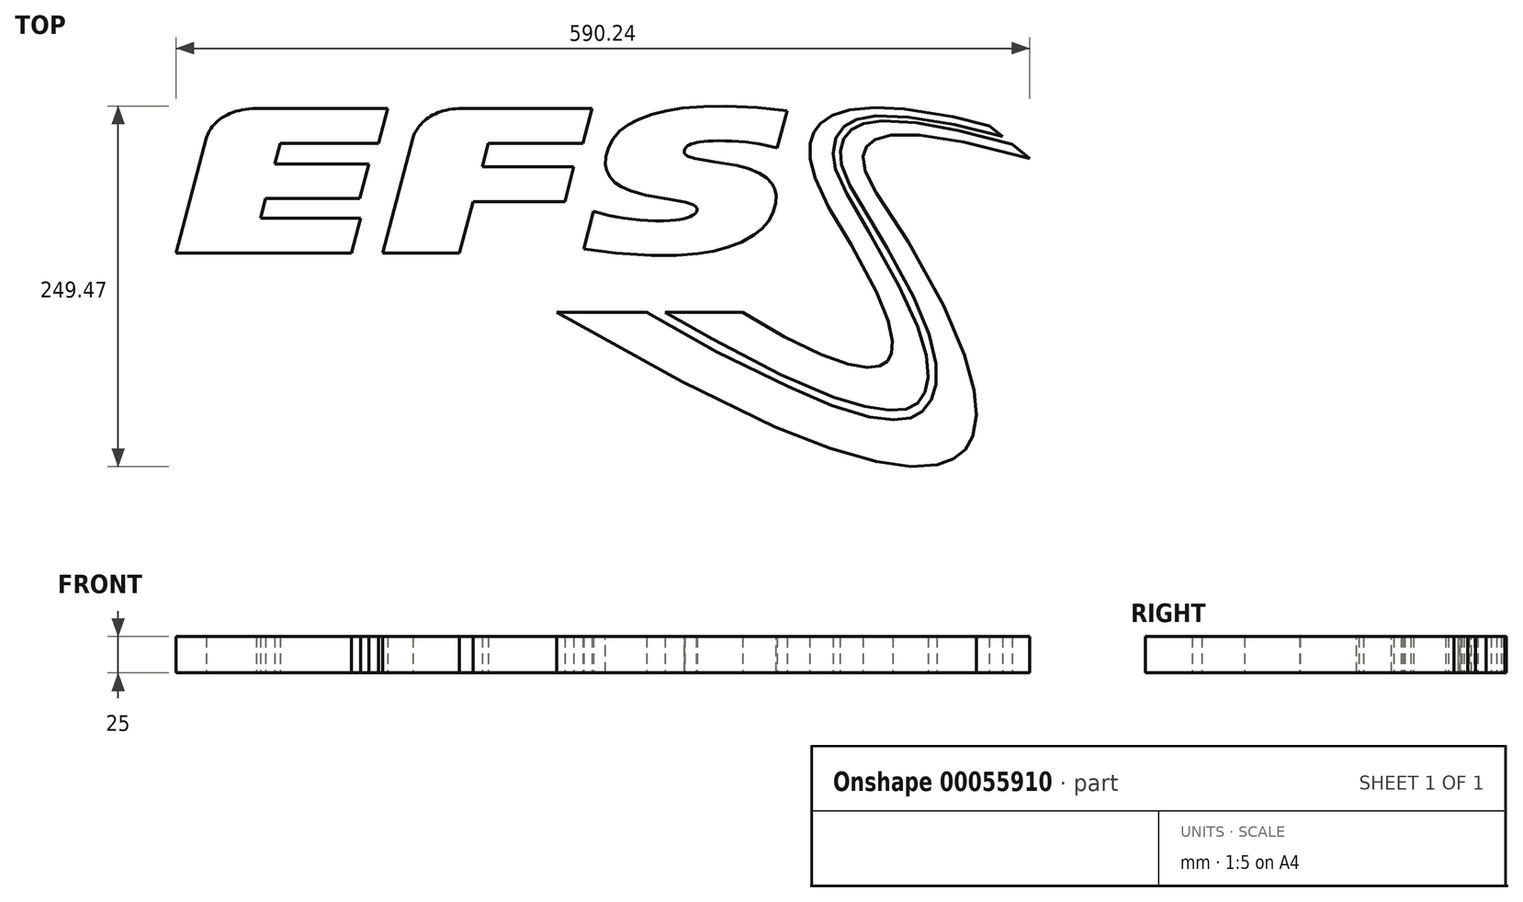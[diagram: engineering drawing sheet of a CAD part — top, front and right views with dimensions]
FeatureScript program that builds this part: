
annotation { "Feature Type Name" : "Feature", "Feature Type Description" : "" }
export const myFeature = defineFeature(function(context is Context, id is Id, definition is map)
    precondition{}
    {
        {
            var Q0;
            Q0=qCreatedBy(makeId("Top.planeOp"),FACE);
            var sketch = newSketch(context, id + "F0", { "sketchPlane" : qUnion([Q0])});
            skLineSegment(sketch, "E0", {"start": v(65.1, 53.07) * mm, "end": v(65.1, 53.21) * mm});
            skLineSegment(sketch, "E1", {"start": v(64.73, 51.46) * mm, "end": v(64.82, 51.68) * mm, "construction": true});
            skLineSegment(sketch, "E2", {"start": v(64.71, 54.56) * mm, "end": v(64.64, 54.68) * mm});
            skLineSegment(sketch, "E3", {"start": v(56.2, 92.99) * mm, "end": v(56.2, 92.8) * mm});
            skLineSegment(sketch, "E4", {"start": v(58.19, 96.78) * mm, "end": v(57.94, 96.57) * mm, "construction": true});
            skLineSegment(sketch, "E5", {"start": v(64.35, 50.82) * mm, "end": v(64.49, 51.03) * mm, "construction": true});
            skLineSegment(sketch, "E6", {"start": v(218.22, -88.53) * mm, "end": v(217.7, -88.86) * mm, "construction": true});
            skLineSegment(sketch, "E7", {"start": v(56.2, 93.18) * mm, "end": v(56.2, 92.99) * mm, "construction": true});
            skLineSegment(sketch, "E8", {"start": v(56.26, 92.44) * mm, "end": v(56.3, 92.26) * mm, "construction": true});
            skLineSegment(sketch, "E9", {"start": v(197.87, -50.41) * mm, "end": v(197.38, -51.11) * mm, "construction": true});
            skLineSegment(sketch, "E10", {"start": v(64.64, 54.68) * mm, "end": v(64.55, 54.8) * mm, "construction": true});
            skLineSegment(sketch, "E11", {"start": v(59.82, 89.37) * mm, "end": v(60.42, 89.17) * mm, "construction": true});
            skLineSegment(sketch, "E12", {"start": v(64.26, 55.14) * mm, "end": v(64.03, 55.36) * mm, "construction": true});
            skLineSegment(sketch, "E13", {"start": v(183.27, 97.87) * mm, "end": v(183.84, 98.45) * mm, "construction": true});
            skLineSegment(sketch, "E14", {"start": v(56.68, 91.43) * mm, "end": v(56.8, 91.28) * mm, "construction": true});
            skLineSegment(sketch, "E15", {"start": v(143.44, 98.9) * mm, "end": v(143.24, 97.48) * mm, "construction": true});
            skLineSegment(sketch, "E16", {"start": v(164.1, 89.26) * mm, "end": v(164.2, 88.02) * mm, "construction": true});
            skLineSegment(sketch, "E17", {"start": v(56.5, 91.75) * mm, "end": v(56.58, 91.6) * mm, "construction": true});
            skLineSegment(sketch, "E18", {"start": v(56.22, 93.37) * mm, "end": v(56.2, 93.18) * mm, "construction": true});
            skLineSegment(sketch, "E19", {"start": v(56.58, 91.6) * mm, "end": v(56.68, 91.43) * mm});
            skLineSegment(sketch, "E20", {"start": v(225.72, -81.26) * mm, "end": v(225.42, -81.7) * mm, "construction": true});
            skLineSegment(sketch, "E21", {"start": v(56.35, 92.09) * mm, "end": v(56.42, 91.92) * mm, "construction": true});
            skLineSegment(sketch, "E22", {"start": v(65, 53.91) * mm, "end": v(64.95, 54.05) * mm, "construction": true});
            skLineSegment(sketch, "E23", {"start": v(173.1, 109.2) * mm, "end": v(172.2, 108.55) * mm, "construction": true});
            skLineSegment(sketch, "E24", {"start": v(182.26, 96.65) * mm, "end": v(182.74, 97.27) * mm, "construction": true});
            skLineSegment(sketch, "E25", {"start": v(56.92, 91.13) * mm, "end": v(57.05, 90.98) * mm, "construction": true});
            skLineSegment(sketch, "E26", {"start": v(200.24, -42.97) * mm, "end": v(200.11, -44.08) * mm, "construction": true});
            skLineSegment(sketch, "E27", {"start": v(196.83, -51.76) * mm, "end": v(196.25, -52.37) * mm, "construction": true});
            skLineSegment(sketch, "E28", {"start": v(64.95, 54.05) * mm, "end": v(64.9, 54.18) * mm, "construction": true});
            skLineSegment(sketch, "E29", {"start": v(63.65, 50.04) * mm, "end": v(63.84, 50.23) * mm, "construction": true});
            skLineSegment(sketch, "E30", {"start": v(56.2, 92.8) * mm, "end": v(56.23, 92.62) * mm, "construction": true});
            skLineSegment(sketch, "E31", {"start": v(56.42, 91.92) * mm, "end": v(56.5, 91.75) * mm, "construction": true});
            skLineSegment(sketch, "E32", {"start": v(56.33, 93.97) * mm, "end": v(56.28, 93.77) * mm});
            skLineSegment(sketch, "E33", {"start": v(184.44, 98.99) * mm, "end": v(185.08, 99.5) * mm, "construction": true});
            skLineSegment(sketch, "E34", {"start": v(64.49, 51.03) * mm, "end": v(64.61, 51.24) * mm, "construction": true});
            skLineSegment(sketch, "E35", {"start": v(-239.63, 122.91) * mm, "end": v(-148.92, 122.91) * mm});
            skLineSegment(sketch, "E36", {"start": v(-155.24, 98.84) * mm, "end": v(-223.24, 98.84) * mm});
            skLineSegment(sketch, "E37", {"start": v(-223.24, 98.84) * mm, "end": v(-226.97, 84.66) * mm});
            skLineSegment(sketch, "E38", {"start": v(-226.97, 84.66) * mm, "end": v(-161.94, 84.66) * mm});
            skLineSegment(sketch, "E39", {"start": v(-155.24, 98.84) * mm, "end": v(-148.92, 122.91) * mm});
            skLineSegment(sketch, "E40", {"start": v(-161.94, 84.66) * mm, "end": v(-168.25, 60.6) * mm});
            skLineSegment(sketch, "E41", {"start": v(-233.28, 60.6) * mm, "end": v(-168.25, 60.6) * mm});
            skLineSegment(sketch, "E42", {"start": v(-233.28, 60.6) * mm, "end": v(-236.85, 46.98) * mm});
            skLineSegment(sketch, "E43", {"start": v(-236.85, 46.98) * mm, "end": v(-167.46, 46.98) * mm});
            skLineSegment(sketch, "E44", {"start": v(-167.46, 46.98) * mm, "end": v(-173.78, 22.91) * mm});
            skLineSegment(sketch, "E45", {"start": v(-173.78, 22.91) * mm, "end": v(-295.12, 22.91) * mm});
            skLineSegment(sketch, "E46", {"start": v(-295.12, 22.91) * mm, "end": v(-274.22, 102.5) * mm});
            skFitSpline(sketch, "E47", {"points": [v(-274.22, 102.5) * mm, v(-273.86, 103.54) * mm, v(-273.35, 104.78) * mm, v(-272.67, 106.18) * mm, v(-271.8, 107.72) * mm, v(-270.74, 109.35) * mm, v(-269.44, 111.03) * mm, v(-267.9, 112.74) * mm, v(-266.09, 114.43) * mm, v(-264, 116.06) * mm, v(-262.83, 116.85) * mm, v(-261.59, 117.6) * mm, v(-260.27, 118.33) * mm, v(-258.86, 119.02) * mm, v(-255.78, 120.28) * mm, v(-252.34, 121.33) * mm, v(-248.52, 122.14) * mm, v(-244.29, 122.69) * mm, v(-239.63, 122.91) * mm], "startDerivative": vector(8.9, 26.32) * mm, "endDerivative": vector(59.2, 1.98) * mm});
            skLineSegment(sketch, "E48", {"start": v(-99.73, 122.91) * mm, "end": v(-7.5, 122.91) * mm});
            skLineSegment(sketch, "E49", {"start": v(-7.5, 122.91) * mm, "end": v(-13.82, 98.84) * mm});
            skLineSegment(sketch, "E50", {"start": v(-13.82, 98.84) * mm, "end": v(-79.24, 98.84) * mm});
            skLineSegment(sketch, "E51", {"start": v(-79.24, 98.84) * mm, "end": v(-83.5, 82.66) * mm});
            skLineSegment(sketch, "E52", {"start": v(-83.5, 82.66) * mm, "end": v(-20.05, 82.66) * mm});
            skLineSegment(sketch, "E53", {"start": v(-20.05, 82.66) * mm, "end": v(-26.37, 58.59) * mm});
            skLineSegment(sketch, "E54", {"start": v(-26.37, 58.59) * mm, "end": v(-89.8, 58.59) * mm});
            skLineSegment(sketch, "E55", {"start": v(-89.8, 58.59) * mm, "end": v(-99.17, 22.91) * mm});
            skLineSegment(sketch, "E56", {"start": v(-99.17, 22.91) * mm, "end": v(-152.3, 22.91) * mm});
            skLineSegment(sketch, "E57", {"start": v(-152.3, 22.91) * mm, "end": v(-131.38, 102.62) * mm});
            skFitSpline(sketch, "E58", {"points": [v(-131.38, 102.62) * mm, v(-131.03, 103.62) * mm, v(-130.55, 104.8) * mm, v(-129.91, 106.13) * mm, v(-129.1, 107.6) * mm, v(-128.11, 109.15) * mm, v(-126.91, 110.76) * mm, v(-125.49, 112.4) * mm, v(-123.83, 114.02) * mm, v(-121.9, 115.62) * mm, v(-119.7, 117.13) * mm, v(-117.21, 118.55) * mm, v(-114.4, 119.83) * mm, v(-111.27, 120.93) * mm, v(-107.8, 121.84) * mm, v(-103.95, 122.51) * mm, v(-99.73, 122.91) * mm], "startDerivative": vector(8, 23.62) * mm, "endDerivative": vector(51.53, 4.1) * mm});
            skLineSegment(sketch, "E59", {"start": v(127.3, 121.2) * mm, "end": v(120.58, 95.55) * mm});
            skLineSegment(sketch, "E60", {"start": v(-6.48, 51.85) * mm, "end": v(-13.28, 25.92) * mm});
            skFitSpline(sketch, "E61", {"points": [v(-6.48, 51.85) * mm, v(-1.42, 50.3) * mm, v(3.92, 48.97) * mm, v(15.43, 46.91) * mm, v(27.44, 45.68) * mm, v(39.38, 45.26) * mm, v(48.5, 45.62) * mm, v(52.63, 46.1) * mm, v(56.35, 46.84) * mm, v(58.02, 47.3) * mm, v(59.55, 47.8) * mm, v(60.93, 48.37) * mm, v(62.16, 48.99) * mm, v(62.72, 49.32) * mm, v(63.2, 49.67) * mm, v(63.65, 50.04) * mm, v(63.84, 50.23) * mm, v(64.03, 50.42) * mm, v(64.2, 50.62) * mm, v(64.35, 50.82) * mm, v(64.49, 51.03) * mm, v(64.61, 51.24) * mm, v(64.73, 51.46) * mm, v(64.82, 51.68) * mm, v(64.9, 51.91) * mm, v(64.97, 52.14) * mm, v(65.04, 52.46) * mm, v(65.09, 52.77) * mm, v(65.1, 53.07) * mm, v(65.1, 53.21) * mm, v(65.1, 53.36) * mm, v(65.08, 53.5) * mm, v(65.06, 53.64) * mm, v(65.03, 53.78) * mm, v(65, 53.91) * mm, v(64.95, 54.05) * mm, v(64.9, 54.18) * mm, v(64.84, 54.3) * mm, v(64.78, 54.43) * mm, v(64.71, 54.56) * mm, v(64.64, 54.68) * mm, v(64.55, 54.8) * mm, v(64.46, 54.92) * mm, v(64.26, 55.14) * mm, v(64.03, 55.36) * mm, v(63.78, 55.57) * mm, v(63.5, 55.78) * mm, v(63.19, 55.97) * mm, v(62.85, 56.15) * mm, v(61.33, 56.84) * mm, v(59.56, 57.48) * mm, v(57.54, 58.06) * mm, v(55.27, 58.59) * mm, v(44.16, 60.45) * mm, v(31.36, 62.67) * mm, v(25, 64.2) * mm, v(18.86, 66.04) * mm, v(15.97, 67.13) * mm, v(13.3, 68.4) * mm, v(12.07, 69.1) * mm, v(10.88, 69.85) * mm, v(9.76, 70.64) * mm, v(8.69, 71.48) * mm, v(7.69, 72.37) * mm, v(6.76, 73.3) * mm, v(5.9, 74.28) * mm, v(5.1, 75.31) * mm, v(4.4, 76.4) * mm, v(3.75, 77.53) * mm, v(3.18, 78.7) * mm, v(2.68, 79.93) * mm, v(2.46, 80.57) * mm, v(2.27, 81.22) * mm, v(2.12, 81.9) * mm, v(1.99, 82.58) * mm, v(1.82, 84.02) * mm, v(1.77, 85.52) * mm, v(1.83, 87.1) * mm, v(2.02, 88.75) * mm, v(2.32, 90.47) * mm, v(2.74, 92.26) * mm, v(3.5, 94.77) * mm, v(4.45, 97.17) * mm, v(5.56, 99.44) * mm, v(6.85, 101.59) * mm, v(8.32, 103.61) * mm, v(9.96, 105.51) * mm, v(11.77, 107.29) * mm, v(13.77, 108.95) * mm, v(15.9, 110.5) * mm, v(18.1, 111.95) * mm, v(20.42, 113.31) * mm, v(22.83, 114.59) * mm, v(27.92, 116.86) * mm, v(33.4, 118.76) * mm, v(39.15, 120.34) * mm, v(45.1, 121.64) * mm, v(51.25, 122.67) * mm, v(57.6, 123.41) * mm, v(70.26, 124.33) * mm, v(82.42, 124.63) * mm, v(105.27, 123.7) * mm, v(127.3, 121.2) * mm], "startDerivative": vector(316.89, -99.49) * mm, "endDerivative": vector(641.52, -85.36) * mm});
            skFitSpline(sketch, "E62", {"points": [v(120.58, 95.55) * mm, v(111.83, 97.6) * mm, v(102.2, 99.2) * mm, v(91.84, 100.23) * mm, v(80.86, 100.57) * mm, v(73.68, 100.42) * mm, v(69.77, 100.15) * mm, v(66.04, 99.63) * mm, v(64.28, 99.27) * mm, v(62.63, 98.83) * mm, v(61.1, 98.3) * mm, v(59.68, 97.7) * mm, v(59.04, 97.36) * mm, v(58.74, 97.18) * mm, v(58.45, 96.98) * mm, v(58.19, 96.78) * mm, v(57.94, 96.57) * mm, v(57.7, 96.35) * mm, v(57.48, 96.12) * mm, v(57.28, 95.89) * mm, v(57.1, 95.64) * mm, v(56.93, 95.38) * mm, v(56.77, 95.12) * mm, v(56.64, 94.85) * mm, v(56.52, 94.56) * mm, v(56.41, 94.27) * mm, v(56.33, 93.97) * mm, v(56.28, 93.77) * mm, v(56.24, 93.57) * mm, v(56.22, 93.37) * mm, v(56.2, 93.18) * mm, v(56.2, 92.99) * mm, v(56.2, 92.8) * mm, v(56.23, 92.62) * mm, v(56.26, 92.44) * mm, v(56.3, 92.26) * mm, v(56.35, 92.09) * mm, v(56.42, 91.92) * mm, v(56.5, 91.75) * mm, v(56.58, 91.6) * mm, v(56.68, 91.43) * mm, v(56.8, 91.28) * mm, v(56.92, 91.13) * mm, v(57.05, 90.98) * mm, v(57.2, 90.83) * mm, v(57.35, 90.7) * mm, v(57.52, 90.55) * mm, v(57.89, 90.29) * mm, v(58.3, 90.04) * mm, v(58.76, 89.8) * mm, v(59.27, 89.58) * mm, v(59.82, 89.37) * mm, v(60.42, 89.17) * mm, v(66.1, 87.76) * mm, v(73.2, 86.52) * mm, v(90.06, 83.87) * mm, v(94.46, 83.01) * mm, v(98.64, 81.94) * mm, v(102.6, 80.65) * mm, v(106.36, 79.15) * mm, v(108.13, 78.3) * mm, v(109.79, 77.37) * mm, v(111.34, 76.37) * mm, v(112.78, 75.28) * mm, v(114.12, 74.1) * mm, v(115.34, 72.86) * mm, v(116.46, 71.53) * mm, v(117.47, 70.12) * mm, v(117.93, 69.38) * mm, v(118.33, 68.61) * mm, v(118.69, 67.81) * mm, v(119, 66.98) * mm, v(119.25, 66.12) * mm, v(119.45, 65.24) * mm, v(119.6, 64.32) * mm, v(119.72, 63.37) * mm, v(119.77, 62.4) * mm, v(119.78, 61.39) * mm, v(119.65, 59.28) * mm, v(119.31, 57.06) * mm, v(118.78, 54.72) * mm, v(118.04, 52.27) * mm, v(117.14, 49.92) * mm, v(116.06, 47.7) * mm, v(114.82, 45.57) * mm, v(113.41, 43.55) * mm, v(111.84, 41.65) * mm, v(110.1, 39.86) * mm, v(108.2, 38.17) * mm, v(106.16, 36.59) * mm, v(104.05, 35.09) * mm, v(99.55, 32.35) * mm, v(94.72, 29.97) * mm, v(89.55, 27.93) * mm, v(84.1, 26.2) * mm, v(78.43, 24.76) * mm, v(72.55, 23.6) * mm, v(66.46, 22.7) * mm, v(54.3, 21.57) * mm, v(42.58, 21.2) * mm, v(14.13, 22.34) * mm, v(-13.28, 25.92) * mm], "startDerivative": vector(-399.88, 100.3) * mm, "endDerivative": vector(-694.86, 108.77) * mm});
            skFitSpline(sketch, "E63", {"points": [v(267, 110.84) * mm, v(259.33, 113.02) * mm, v(239.74, 117.7) * mm, v(213.42, 122.16) * mm, v(199.35, 123.43) * mm, v(192.38, 123.68) * mm, v(185.55, 123.6) * mm, v(178.95, 123.18) * mm, v(172.65, 122.35) * mm, v(166.75, 121.07) * mm, v(163.97, 120.25) * mm, v(161.31, 119.3) * mm, v(158.8, 118.22) * mm, v(156.43, 117) * mm, v(154.22, 115.64) * mm, v(152.18, 114.12) * mm, v(151.22, 113.3) * mm, v(150.31, 112.46) * mm, v(149.45, 111.56) * mm, v(148.64, 110.63) * mm, v(147.87, 109.65) * mm, v(147.16, 108.64) * mm, v(146.5, 107.58) * mm, v(145.9, 106.47) * mm, v(145.34, 105.33) * mm, v(144.84, 104.13) * mm, v(144.4, 102.9) * mm, v(144.02, 101.61) * mm, v(143.7, 100.28) * mm, v(143.44, 98.9) * mm, v(143.24, 97.48) * mm, v(143.1, 96) * mm, v(143.03, 92.9) * mm, v(143.22, 89.6) * mm, v(143.7, 86.1) * mm, v(144.46, 82.37) * mm, v(145.53, 78.43) * mm, v(146.9, 74.26) * mm, v(150.62, 65.23) * mm, v(155.7, 55.24) * mm, v(162.2, 44.23) * mm, v(178.55, 16.87) * mm, v(190.01, -5.44) * mm, v(194.05, -14.82) * mm, v(197.05, -23.1) * mm, v(199.05, -30.32) * mm, v(199.7, -33.55) * mm, v(200.13, -36.54) * mm, v(200.33, -39.28) * mm, v(200.32, -41.8) * mm, v(200.24, -42.97) * mm, v(200.11, -44.08) * mm, v(199.93, -45.15) * mm, v(199.7, -46.15) * mm, v(199.43, -47.1) * mm, v(199.1, -48.01) * mm, v(198.74, -48.86) * mm, v(198.33, -49.66) * mm, v(197.87, -50.41) * mm, v(197.38, -51.11) * mm, v(196.83, -51.76) * mm, v(196.25, -52.37) * mm, v(195.63, -52.93) * mm, v(194.97, -53.44) * mm, v(194.27, -53.9) * mm, v(193.53, -54.33) * mm, v(192.76, -54.7) * mm, v(191.95, -55.04) * mm, v(191.1, -55.34) * mm, v(190.23, -55.59) * mm, v(189.32, -55.8) * mm, v(188.38, -55.97) * mm, v(186.4, -56.2) * mm, v(184.3, -56.29) * mm, v(182.1, -56.23) * mm, v(179.79, -56.03) * mm, v(177.39, -55.71) * mm, v(172.32, -54.7) * mm, v(166.96, -53.26) * mm, v(161.36, -51.42) * mm, v(149.69, -46.8) * mm, v(137.75, -41.24) * mm, v(114.97, -29) * mm, v(96.71, -17.98) * mm], "startDerivative": vector(-382.9, 112.02) * mm, "endDerivative": vector(-585.56, 364.37) * mm});
            skLineSegment(sketch, "E64", {"start": v(96.71, -17.98) * mm, "end": v(42.95, -18.04) * mm});
            skLineSegment(sketch, "E65", {"start": v(30.23, -18) * mm, "end": v(-31.93, -17.98) * mm});
            skFitSpline(sketch, "E66", {"points": [v(42.95, -18.04) * mm, v(57.24, -26.11) * mm, v(98.6, -48.93) * mm, v(137.66, -67.77) * mm, v(160.05, -76.9) * mm, v(172.01, -80.94) * mm, v(178.11, -82.6) * mm, v(184.26, -83.96) * mm, v(191.65, -85.18) * mm, v(195.26, -85.6) * mm, v(198.78, -85.83) * mm, v(202.19, -85.85) * mm, v(205.46, -85.63) * mm, v(207.03, -85.42) * mm, v(208.56, -85.13) * mm, v(210.05, -84.77) * mm, v(211.48, -84.32) * mm, v(212.85, -83.8) * mm, v(214.17, -83.17) * mm, v(215.43, -82.46) * mm, v(216.63, -81.64) * mm, v(217.76, -80.73) * mm, v(218.81, -79.7) * mm, v(219.8, -78.57) * mm, v(220.7, -77.32) * mm, v(221.54, -75.96) * mm, v(222.28, -74.47) * mm, v(222.94, -72.85) * mm, v(223.5, -71.1) * mm, v(223.98, -69.22) * mm, v(224.36, -67.2) * mm, v(224.65, -65.02) * mm, v(224.82, -62.7) * mm, v(224.9, -59.9) * mm, v(224.85, -57.14) * mm, v(224.38, -51.73) * mm, v(223.5, -46.47) * mm, v(222.26, -41.36) * mm, v(219.03, -31.54) * mm, v(215.28, -22.21) * mm, v(206.6, -3.34) * mm, v(197.07, 14.55) * mm, v(176.68, 49.81) * mm, v(171.7, 58.36) * mm, v(166.05, 68.74) * mm, v(163.48, 74.2) * mm, v(161.33, 79.63) * mm, v(160.48, 82.28) * mm, v(159.82, 84.86) * mm, v(159.36, 87.35) * mm, v(159.22, 88.55) * mm, v(159.14, 89.73) * mm, v(159.1, 92.3) * mm, v(159.22, 94.73) * mm, v(159.49, 97) * mm, v(159.9, 99.12) * mm, v(160.45, 101.1) * mm, v(161.14, 102.94) * mm, v(161.95, 104.65) * mm, v(162.88, 106.22) * mm, v(163.91, 107.67) * mm, v(165.06, 109) * mm, v(166.3, 110.22) * mm, v(167.64, 111.33) * mm, v(169.06, 112.33) * mm, v(170.56, 113.23) * mm, v(172.14, 114.03) * mm, v(173.78, 114.74) * mm, v(175.48, 115.37) * mm, v(177.23, 115.91) * mm, v(180.88, 116.78) * mm, v(184.65, 117.37) * mm, v(188.52, 117.73) * mm, v(196.29, 117.92) * mm, v(203.77, 117.64) * mm, v(218.55, 116.15) * mm, v(234.7, 113.5) * mm, v(265.49, 106.41) * mm, v(276.23, 103.44) * mm], "startDerivative": vector(518.26, -292.6) * mm, "endDerivative": vector(453.15, -133.16) * mm});
            skLineSegment(sketch, "E67", {"start": v(267, 110.84) * mm, "end": v(276.23, 103.44) * mm});
            skLineSegment(sketch, "E68", {"start": v(295.12, 88.38) * mm, "end": v(283.09, 98.03) * mm});
            skFitSpline(sketch, "E69", {"points": [v(283.09, 98.03) * mm, v(258.08, 104.83) * mm, v(233.32, 110.4) * mm, v(221.27, 112.42) * mm, v(209.55, 113.76) * mm, v(198.26, 114.28) * mm, v(192.8, 114.2) * mm, v(187.49, 113.88) * mm, v(185.38, 113.64) * mm, v(183.25, 113.27) * mm, v(181.13, 112.77) * mm, v(179.03, 112.12) * mm, v(176.97, 111.31) * mm, v(174.99, 110.34) * mm, v(174.03, 109.8) * mm, v(173.1, 109.2) * mm, v(172.2, 108.55) * mm, v(171.32, 107.86) * mm, v(170.49, 107.12) * mm, v(169.69, 106.33) * mm, v(168.93, 105.49) * mm, v(168.22, 104.6) * mm, v(167.55, 103.65) * mm, v(166.93, 102.64) * mm, v(166.37, 101.58) * mm, v(165.86, 100.46) * mm, v(165.4, 99.28) * mm, v(165.01, 98.04) * mm, v(164.68, 96.74) * mm, v(164.42, 95.37) * mm, v(164.23, 93.95) * mm, v(164.11, 92.45) * mm, v(164.07, 90.89) * mm, v(164.1, 89.26) * mm, v(164.2, 88.02) * mm, v(164.4, 86.71) * mm, v(165, 83.96) * mm, v(165.88, 81.1) * mm, v(166.94, 78.19) * mm, v(169.38, 72.6) * mm, v(171.81, 67.9) * mm, v(199.2, 21.87) * mm, v(212.15, -1.76) * mm, v(218.06, -14.23) * mm, v(223.45, -27.33) * mm, v(227.29, -38.69) * mm, v(229.03, -45.5) * mm, v(230.32, -52.72) * mm, v(230.7, -56.43) * mm, v(230.89, -60.15) * mm, v(230.82, -63.87) * mm, v(230.48, -67.54) * mm, v(229.83, -71.15) * mm, v(229.38, -72.92) * mm, v(228.84, -74.66) * mm, v(228.21, -76.36) * mm, v(227.48, -78.04) * mm, v(226.65, -79.67) * mm, v(225.72, -81.26) * mm, v(225.42, -81.7) * mm, v(225.05, -82.18) * mm, v(224.13, -83.24) * mm, v(221.83, -85.56) * mm, v(219.35, -87.69) * mm, v(218.22, -88.53) * mm, v(217.7, -88.86) * mm, v(217.23, -89.13) * mm, v(216.18, -89.64) * mm, v(215.1, -90.1) * mm, v(212.86, -90.91) * mm, v(210.5, -91.54) * mm, v(208.03, -92) * mm, v(205.46, -92.3) * mm, v(202.8, -92.46) * mm, v(200.06, -92.47) * mm, v(197.24, -92.35) * mm, v(191.4, -91.73) * mm, v(185.36, -90.67) * mm, v(172.88, -87.45) * mm, v(160.31, -83.18) * mm, v(148.14, -78.36) * mm, v(126.98, -69.02) * mm, v(77.38, -44.74) * mm, v(30.23, -18) * mm], "startDerivative": vector(-827.81, 234.5) * mm, "endDerivative": vector(-1064.6, 627.38) * mm});
            skFitSpline(sketch, "E70", {"points": [v(-31.93, -17.98) * mm, v(87.61, -82.96) * mm, v(134.03, -103.59) * mm, v(153.98, -111.12) * mm, v(171.88, -116.9) * mm, v(187.8, -121.05) * mm, v(201.86, -123.64) * mm, v(208.2, -124.38) * mm, v(214.11, -124.76) * mm, v(219.6, -124.8) * mm, v(224.66, -124.5) * mm, v(229.32, -123.9) * mm, v(233.59, -122.97) * mm, v(235.58, -122.4) * mm, v(237.47, -121.75) * mm, v(239.28, -121.03) * mm, v(240.99, -120.24) * mm, v(242.6, -119.38) * mm, v(244.14, -118.45) * mm, v(245.58, -117.46) * mm, v(246.94, -116.4) * mm, v(248.21, -115.28) * mm, v(249.4, -114.1) * mm, v(250.5, -112.85) * mm, v(251.53, -111.55) * mm, v(252.48, -110.19) * mm, v(253.35, -108.77) * mm, v(254.14, -107.3) * mm, v(254.86, -105.77) * mm, v(255.5, -104.2) * mm, v(256.07, -102.57) * mm, v(257, -99.16) * mm, v(257.65, -95.58) * mm, v(258.04, -91.81) * mm, v(258.18, -87.89) * mm, v(258.08, -83.81) * mm, v(257.74, -79.6) * mm, v(257.2, -75.25) * mm, v(255.47, -66.2) * mm, v(253, -56.8) * mm, v(249.87, -47.08) * mm, v(241.98, -27.16) * mm, v(232.5, -7.15) * mm, v(211.52, 30.2) * mm, v(192.54, 59.2) * mm, v(188.07, 65.95) * mm, v(184.61, 72.06) * mm, v(183.25, 74.88) * mm, v(182.12, 77.54) * mm, v(181.22, 80.06) * mm, v(180.54, 82.44) * mm, v(180.07, 84.67) * mm, v(179.8, 86.77) * mm, v(179.76, 87.77) * mm, v(179.75, 88.73) * mm, v(179.8, 89.66) * mm, v(179.89, 90.56) * mm, v(180.03, 91.43) * mm, v(180.21, 92.27) * mm, v(180.45, 93.07) * mm, v(180.72, 93.85) * mm, v(181.04, 94.6) * mm, v(181.4, 95.3) * mm, v(181.8, 96) * mm, v(182.26, 96.65) * mm, v(182.74, 97.27) * mm, v(183.27, 97.87) * mm, v(183.84, 98.45) * mm, v(184.44, 98.99) * mm, v(185.08, 99.5) * mm, v(185.76, 100) * mm, v(186.48, 100.46) * mm, v(187.23, 100.9) * mm, v(188.83, 101.7) * mm, v(190.56, 102.41) * mm, v(192.41, 103.02) * mm, v(194.38, 103.54) * mm, v(196.47, 103.98) * mm, v(198.65, 104.33) * mm, v(203.32, 104.79) * mm, v(208.32, 104.95) * mm, v(213.6, 104.85) * mm, v(224.84, 103.93) * mm, v(236.6, 102.27) * mm, v(260.06, 97.52) * mm, v(295.12, 88.38) * mm], "startDerivative": vector(2079.23, -1169.23) * mm, "endDerivative": vector(1107.63, -302.93) * mm});
            skSolve(sketch);
        }
        {
            var Q0;
            Q0 = qSketchRegion(id + "F0", true);
            extrude(context, id + "F1", {"entities" : qUnion([Q0]), "depth" : 25 * mm});
        }
    });
